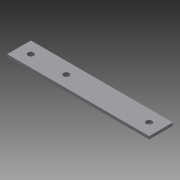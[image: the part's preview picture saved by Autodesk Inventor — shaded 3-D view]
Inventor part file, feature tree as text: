
AUTODESK INVENTOR PART (.ipt)
format: ipt  version: 2013 (Build 170138000, 138)  size: 84,480 bytes
history: native  units: in
note: dims shown in document units (in); Inventor stores cm internally (conversion verified against a paired STEP export)
features: extrude x2, sketch x2
ambient origin geometry x8: Origin, YZ Plane, XZ Plane, XY Plane, X Axis, Y Axis, Z Axis, Center Point
bodies: Solid1 (feature_tree)
feature tree (4):
  extrude  "Extrusion1"  Depth=1.0in
  extrude  "Extrusion2"  TaperAngle=0.0deg  [1 undecoded]
  sketch  "Sketch1"  dims[d0=6.0in d1=1.0in]
  sketch  "Sketch2"  dims[d2=0.5in d3=0.0in d4=1.0in d5=180.0deg d6=1.0in d7=0.25in d8=0.25in d9=0.125in d10=0.0in d11=0.25in d12=1.0in d13=0.0in]
note: 1 required parameter value undecoded (feature->parameter linkage not recoverable at this tier; creation-order binding heuristic only, values carry confidence <= 0.55)
